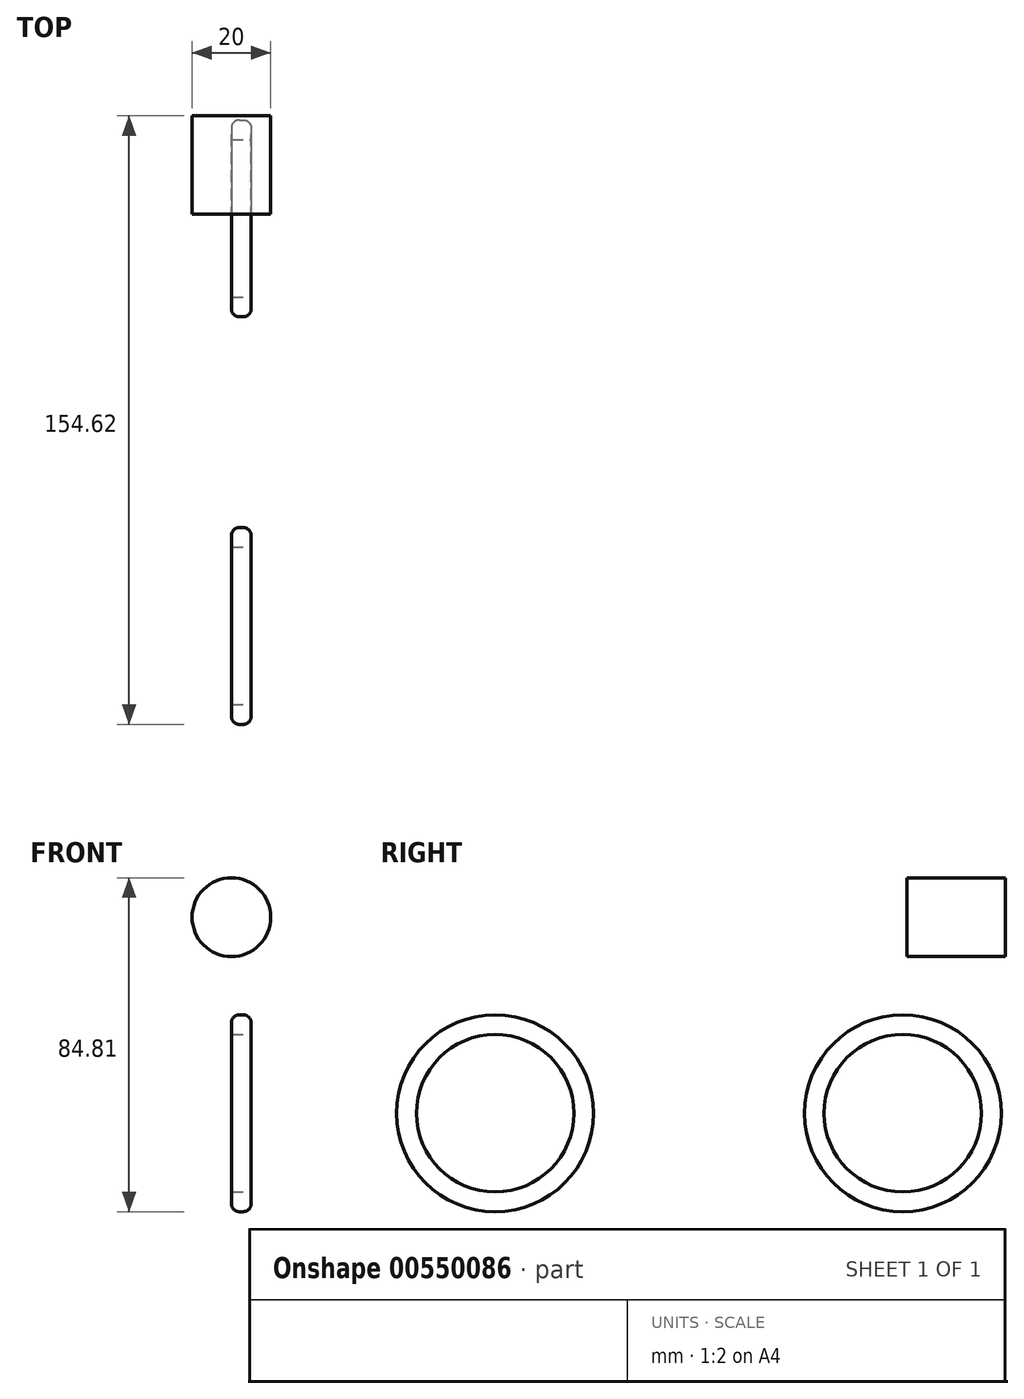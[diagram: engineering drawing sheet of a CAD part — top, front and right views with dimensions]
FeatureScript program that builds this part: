
annotation { "Feature Type Name" : "Feature", "Feature Type Description" : "" }
export const myFeature = defineFeature(function(context is Context, id is Id, definition is map)
    precondition{}
    {
        {
            var Q0;
            Q0=qCreatedBy(makeId("Right.planeOp"),FACE);
            var sketch = newSketch(context, id + "F0", { "sketchPlane" : qUnion([Q0])});
            skCircle(sketch, "E0", {"center": v(-50.52, -36.7) * mm, "radius": 25 * mm});
            skCircle(sketch, "E1", {"center": v(53.04, -36.7) * mm, "radius": 25 * mm});
            skLineSegment(sketch, "E2", {"start": v(-50.52, -36.7) * mm, "end": v(-50.52, -75.15) * mm});
            skLineSegment(sketch, "E3", {"start": v(-50.52, -75.15) * mm, "end": v(-50.52, 0) * mm});
            skCircle(sketch, "E4", {"center": v(-50.52, -36.7) * mm, "radius": 20 * mm});
            skCircle(sketch, "E5", {"center": v(53.04, -36.7) * mm, "radius": 20 * mm});
            skLineSegment(sketch, "E6", {"start": v(53.04, -36.7) * mm, "end": v(53.04, -67.36) * mm});
            skLineSegment(sketch, "E7", {"start": v(53.04, -67.36) * mm, "end": v(53.04, 4.18) * mm});
            skSolve(sketch);
        }
        {
            var Q0;
            Q0=qCreatedBy(makeId("Front.planeOp"),FACE);
            var sketch = newSketch(context, id + "F1", { "sketchPlane" : qUnion([Q0])});
            skLineSegment(sketch, "E8.0", {"start": v(0, -11.7) * mm, "end": v(0, -61.7) * mm});
            skLineSegment(sketch, "E9.0", {"start": v(0, -16.7) * mm, "end": v(0, -56.7) * mm});
            skArc(sketch, "E10", {"start": v(0, -16.7) * mm, "mid": v(5, -11.7) * mm, "end": v(0, -6.7) * mm});
            skLineSegment(sketch, "E11", {"start": v(0, -11.7) * mm, "end": v(5, -11.7) * mm});
            skLineSegment(sketch, "E12", {"start": v(0, -16.7) * mm, "end": v(0, -2.98) * mm});
            skPoint(sketch, "E13.orphan", {"position": v(-5, -11.7) * mm});
            skSolve(sketch);
        }
        {
            var Q0;
            {var subQ0=sQuery(id+"F0.wireOp",EDGE,"E3");var subQ1=sQuery(id+"F0.wireOp",EDGE,"E0");var subQ2=makeQuery(id+"F0.imprint","INTERSECT",VERTEX,{"disambiguationData":[OD(0.0)],"derivedFrom":[subQ1,subQ0]});Q0=makeQuery(id+"F0.imprint","IMPRINT",FACE,{"disambiguationData":[TD([[makeQuery(id+"F0.imprint","IMPRINT",EDGE,{"disambiguationData":[TD([[subQ2,1.0]])],"derivedFrom":subQ1}),1.0]])]});}
            var Q1;
            {var subQ0=sQuery(id+"F0.wireOp",EDGE,"E3");var subQ1=sQuery(id+"F0.wireOp",EDGE,"E0");var subQ2=makeQuery(id+"F0.imprint","INTERSECT",VERTEX,{"disambiguationData":[OD(0.0)],"derivedFrom":[subQ1,subQ0]});Q1=makeQuery(id+"F0.imprint","IMPRINT",FACE,{"disambiguationData":[TD([[makeQuery(id+"F0.imprint","IMPRINT",EDGE,{"disambiguationData":[TD([[subQ2,-1.0]])],"derivedFrom":subQ1}),1.0]])]});}
            var Q2;
            {var subQ0=sQuery(id+"F0.wireOp",EDGE,"E7");var subQ1=sQuery(id+"F0.wireOp",EDGE,"E1");var subQ2=makeQuery(id+"F0.imprint","INTERSECT",VERTEX,{"disambiguationData":[OD(0.0)],"derivedFrom":[subQ1,subQ0]});Q2=makeQuery(id+"F0.imprint","IMPRINT",FACE,{"disambiguationData":[TD([[makeQuery(id+"F0.imprint","IMPRINT",EDGE,{"disambiguationData":[TD([[subQ2,-1.0]])],"derivedFrom":subQ1}),1.0]])]});}
            var Q3;
            {var subQ0=sQuery(id+"F0.wireOp",EDGE,"E7");var subQ1=sQuery(id+"F0.wireOp",EDGE,"E1");var subQ2=makeQuery(id+"F0.imprint","INTERSECT",VERTEX,{"disambiguationData":[OD(0.0)],"derivedFrom":[subQ1,subQ0]});Q3=makeQuery(id+"F0.imprint","IMPRINT",FACE,{"disambiguationData":[TD([[makeQuery(id+"F0.imprint","IMPRINT",EDGE,{"disambiguationData":[TD([[subQ2,1.0]])],"derivedFrom":subQ1}),1.0]])]});}
            var Q4;
            Q4=sQuery(id+"F1.wireOp",EDGE,"E11");
            sweep(context, id + "F2", {"profiles" : qUnion([Q0, Q1, Q2, Q3]), "path" : qUnion([Q4])});
        }
        {
            var Q0;
            Q0=makeQuery(id+"F2.opSweep","CAP_EDGE",EDGE,{"disambiguationData":[OSD([sQuery(id+"F0.wireOp",EDGE,"E0"),sQuery(id+"F1.wireOp",VERTEX,"E11.end")])],"isStart":false});
            fillet(context, id + "F3", {"entities" : qUnion([Q0]), "radius" : 2 * mm, "tangentPropagation" : true, "allowEdgeOverflow" : false});
        }
        {
            var Q0;
            Q0=makeQuery(id+"F2.opSweep","CAP_EDGE",EDGE,{"disambiguationData":[OSD([sQuery(id+"F0.wireOp",EDGE,"E0"),sQuery(id+"F1.wireOp",VERTEX,"E11.start")])],"isStart":true});
            fillet(context, id + "F4", {"entities" : qUnion([Q0]), "radius" : 2 * mm, "tangentPropagation" : true, "allowEdgeOverflow" : false});
        }
        {
            var Q0;
            Q0=makeQuery(id+"F2.opSweep","CAP_EDGE",EDGE,{"disambiguationData":[OSD([sQuery(id+"F0.wireOp",EDGE,"E1"),sQuery(id+"F1.wireOp",VERTEX,"E11.end")])],"isStart":false});
            fillet(context, id + "F5", {"entities" : qUnion([Q0]), "radius" : 2 * mm, "tangentPropagation" : true, "allowEdgeOverflow" : false});
        }
        {
            var Q0;
            Q0=makeQuery(id+"F2.opSweep","CAP_EDGE",EDGE,{"disambiguationData":[OSD([sQuery(id+"F0.wireOp",EDGE,"E1"),sQuery(id+"F1.wireOp",VERTEX,"E11.start")])],"isStart":true});
            fillet(context, id + "F6", {"entities" : qUnion([Q0]), "radius" : 2 * mm, "tangentPropagation" : true, "allowEdgeOverflow" : false});
        }
        {
            var Q0;
            Q0=qCreatedBy(makeId("Front.planeOp"),FACE);
            var sketch = newSketch(context, id + "F7", { "sketchPlane" : qUnion([Q0])});
            skCircle(sketch, "E14", {"center": v(0, 13.11) * mm, "radius": 10 * mm});
            skSolve(sketch);
        }
        {
            var Q0;
            Q0=makeQuery(id+"F7.imprint","IMPRINT",FACE,{"disambiguationData":[TD([[makeQuery(id+"F7.imprint","IMPRINT",EDGE,{"derivedFrom":sQuery(id+"F7.wireOp",EDGE,"E14")}),1.0]])]});
            extrude(context, id + "F8", {"entities" : qUnion([Q0]), "depth" : 25 * mm, "offsetDistance" : 25 * mm});
        }
        {
            var Q0;
            Q0=makeQuery(id+"F8.opExtrude","SWEPT_BODY",BODY,{"disambiguationData":[OSD([sQuery(id+"F7.wireOp",EDGE,"E14")])]});
            transform(context, id + "F9", {"entities" : qUnion([Q0]), "transformType" : TransformType.TRANSLATION_3D, "dx" : 0 * mm, "dy" : 79.1 * mm, "dz" : 0 * mm, "makeCopy" : false});
        }
    });
